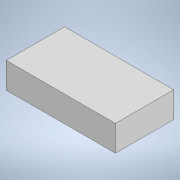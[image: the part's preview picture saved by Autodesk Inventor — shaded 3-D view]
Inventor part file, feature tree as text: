
AUTODESK INVENTOR PART (.ipt)
format: ipt  version: 2021 (Build 250183000, 183)  size: 88,576 bytes
history: native  units: mm
features: extrude x1, sketch x1
ambient origin geometry x8: Origin, YZ Plane, XZ Plane, XY Plane, X Axis, Y Axis, Z Axis, Center Point
bodies: Solid1 (feature_tree)
feature tree (2):
  extrude  "Extrusion1"  Depth=31.5mm
  sketch  "Sketch1"  dims[d0=59.0mm d1=31.5mm d2=14.0mm d3=0.0mm]
